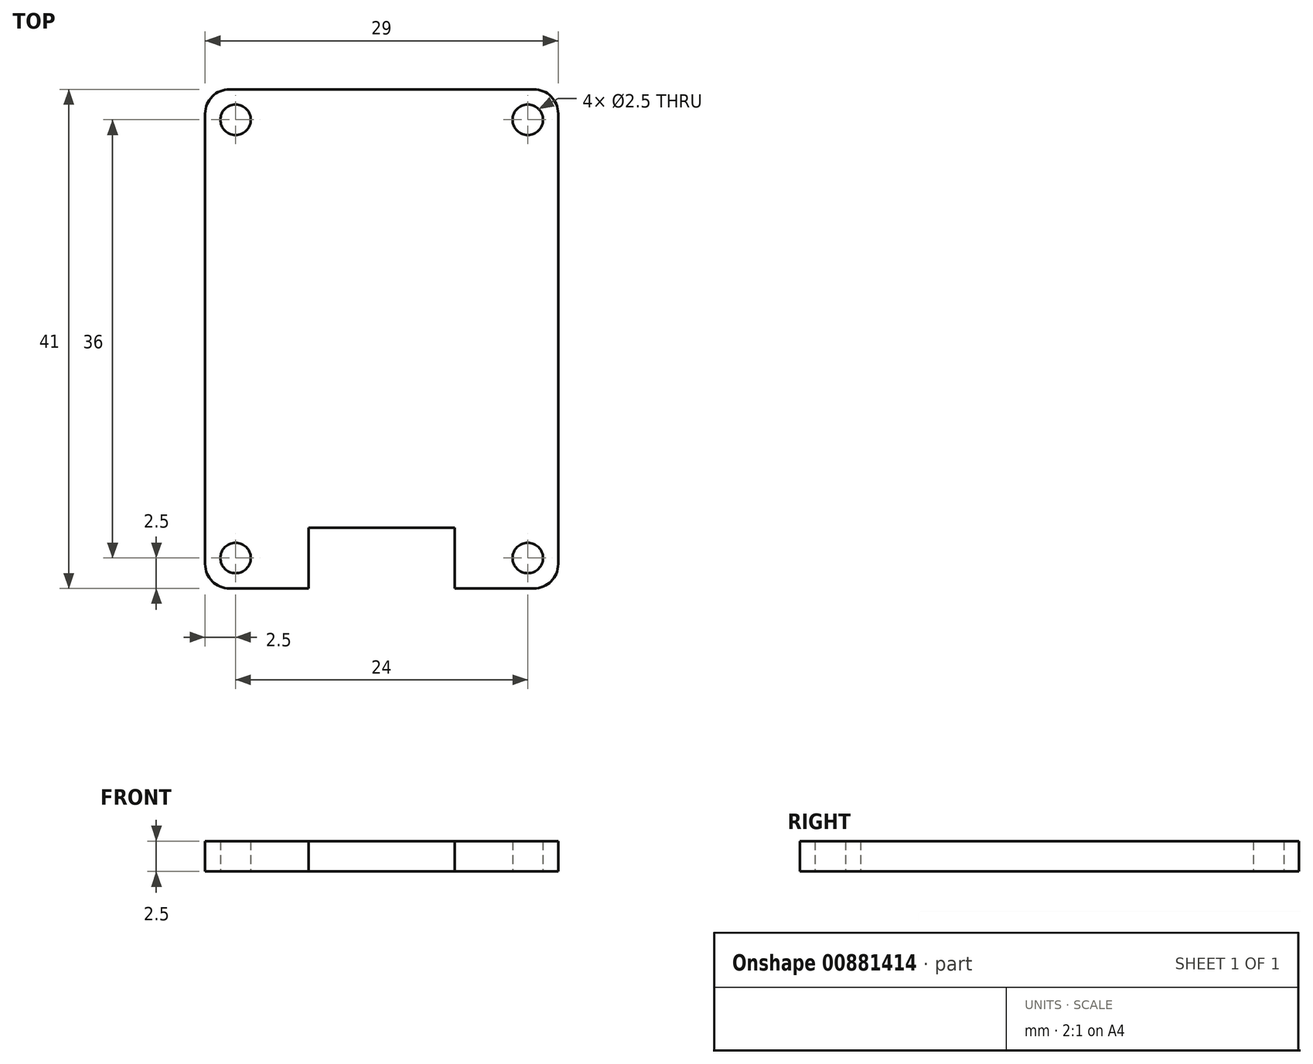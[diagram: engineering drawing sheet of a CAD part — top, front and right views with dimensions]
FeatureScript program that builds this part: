
annotation { "Feature Type Name" : "Feature", "Feature Type Description" : "" }
export const myFeature = defineFeature(function(context is Context, id is Id, definition is map)
    precondition{}
    {
        {
            var Q0;
            Q0=qCreatedBy(makeId("Top.planeOp"),FACE);
            var sketch = newSketch(context, id + "F0", { "sketchPlane" : qUnion([Q0])});
            skLineSegment(sketch, "E0.bottom", {"start": v(8.5, -16) * mm, "end": v(-10.5, -16) * mm});
            skLineSegment(sketch, "E0.top", {"start": v(8.5, 15) * mm, "end": v(-10.5, 15) * mm});
            skLineSegment(sketch, "E0.left", {"start": v(8.5, -16) * mm, "end": v(8.5, 15) * mm});
            skLineSegment(sketch, "E0.right", {"start": v(-10.5, -16) * mm, "end": v(-10.5, 15) * mm});
            skPoint(sketch, "E0.middle", {"position": v(-1, -0.5) * mm});
            skLineSegment(sketch, "E1.0", {"start": v(13.5, 20) * mm, "end": v(-15.5, 20) * mm});
            skLineSegment(sketch, "E1.1", {"start": v(13.5, -21) * mm, "end": v(13.5, 20) * mm});
            skLineSegment(sketch, "E1.2", {"start": v(13.5, -21) * mm, "end": v(-15.5, -21) * mm});
            skLineSegment(sketch, "E1.3", {"start": v(-15.5, -21) * mm, "end": v(-15.5, 20) * mm});
            skPoint(sketch, "E2", {"position": v(11, 17.5) * mm});
            skPoint(sketch, "E3", {"position": v(-13, 17.5) * mm});
            skPoint(sketch, "E4", {"position": v(-13, -18.5) * mm});
            skPoint(sketch, "E5", {"position": v(11, -18.5) * mm});
            skCircle(sketch, "E6", {"center": v(-13, -18.5) * mm, "radius": 1.25 * mm});
            skCircle(sketch, "E7", {"center": v(11, -18.5) * mm, "radius": 1.25 * mm});
            skCircle(sketch, "E8", {"center": v(11, 17.5) * mm, "radius": 1.25 * mm});
            skCircle(sketch, "E9", {"center": v(-13, 17.5) * mm, "radius": 1.25 * mm});
            skPoint(sketch, "E10", {"position": v(5, -16) * mm});
            skPoint(sketch, "E11", {"position": v(-7, -16) * mm});
            skLineSegment(sketch, "E12", {"start": v(-7, -16) * mm, "end": v(-7, -21) * mm});
            skLineSegment(sketch, "E13", {"start": v(5, -16) * mm, "end": v(5, -21) * mm});
            skSolve(sketch);
        }
        {
            var Q0;
            {var subQ4=sQuery(id+"F0.wireOp",EDGE,"E0.bottom");Q0=makeQuery(id+"F0.imprint","IMPRINT",FACE,{"disambiguationData":[TD([[makeQuery(id+"F0.imprint","IMPRINT",EDGE,{"derivedFrom":subQ4}),1.0]])]});}
            var Q1;
            {var subQ1=sQuery(id+"F0.wireOp",EDGE,"E0.bottom");Q1=makeQuery(id+"F0.imprint","IMPRINT",FACE,{"disambiguationData":[TD([[makeQuery(id+"F0.imprint","IMPRINT",EDGE,{"derivedFrom":subQ1}),-1.0]])]});}
            extrude(context, id + "F1", {"entities" : qUnion([Q0, Q1]), "depth" : 2.5 * mm, "offsetDistance" : 25 * mm});
        }
        {
            var Q0;
            Q0=makeQuery(id+"F1.opExtrude","SWEPT_EDGE",EDGE,{"disambiguationData":[OSD([sQuery(id+"F0.wireOp",EDGE,"E1.0"),sQuery(id+"F0.wireOp",EDGE,"E1.3")])]});
            var Q1;
            Q1=makeQuery(id+"F1.opExtrude","SWEPT_EDGE",EDGE,{"disambiguationData":[OSD([sQuery(id+"F0.wireOp",EDGE,"E1.0"),sQuery(id+"F0.wireOp",EDGE,"E1.1")])]});
            var Q2;
            Q2=makeQuery(id+"F1.opExtrude","SWEPT_EDGE",EDGE,{"disambiguationData":[OSD([sQuery(id+"F0.wireOp",EDGE,"E1.1"),sQuery(id+"F0.wireOp",EDGE,"E1.2")])]});
            var Q3;
            Q3=makeQuery(id+"F1.opExtrude","SWEPT_EDGE",EDGE,{"disambiguationData":[OSD([sQuery(id+"F0.wireOp",EDGE,"E1.2"),sQuery(id+"F0.wireOp",EDGE,"E1.3")])]});
            fillet(context, id + "F2", {"entities" : qUnion([Q0, Q1, Q2, Q3]), "tangentPropagation" : true, "radius" : 2 * mm, "defaultsChanged" : true, "vertexSettings" : [], "allowEdgeOverflow" : false});
        }
    });
